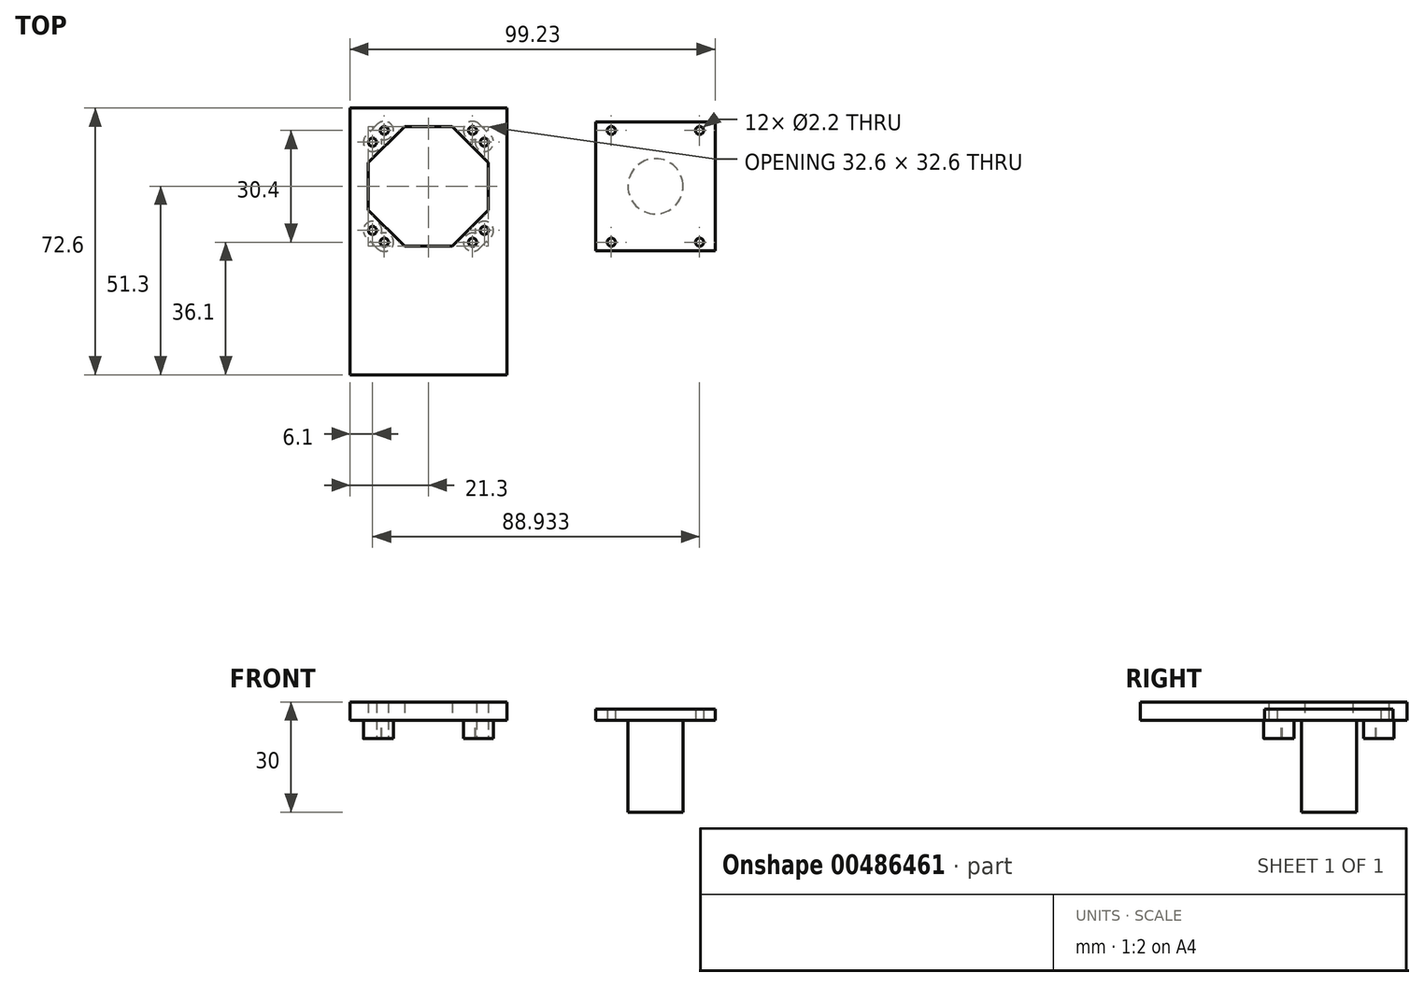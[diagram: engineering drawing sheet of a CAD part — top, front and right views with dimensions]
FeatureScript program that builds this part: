
annotation { "Feature Type Name" : "Feature", "Feature Type Description" : "" }
export const myFeature = defineFeature(function(context is Context, id is Id, definition is map)
    precondition{}
    {
        {
            assignVariable(context, id + "F0", {"name" : "spacer_height", "anyValue" : 5});
        }
        {
            var Q0;
            Q0=qCreatedBy(makeId("Top.planeOp"),FACE);
            var sketch = newSketch(context, id + "F1", { "sketchPlane" : qUnion([Q0])});
            skCircle(sketch, "E0", {"center": v(-12, 15.2) * mm, "radius": 1.1 * mm, "construction": true});
            skCircle(sketch, "E1", {"center": v(-15.2, 12) * mm, "radius": 1.1 * mm, "construction": true});
            skCircle(sketch, "E2.MirrorC", {"center": v(15.2, 12) * mm, "radius": 1.1 * mm, "construction": true});
            skCircle(sketch, "E3.MirrorC", {"center": v(12, 15.2) * mm, "radius": 1.1 * mm, "construction": true});
            skCircle(sketch, "E4.MirrorC", {"center": v(-12, -15.2) * mm, "radius": 1.1 * mm, "construction": true});
            skCircle(sketch, "E5.MirrorC", {"center": v(-15.2, -12) * mm, "radius": 1.1 * mm, "construction": true});
            skCircle(sketch, "E6.MirrorC", {"center": v(12, -15.2) * mm, "radius": 1.1 * mm, "construction": true});
            skCircle(sketch, "E7.MirrorC", {"center": v(15.2, -12) * mm, "radius": 1.1 * mm, "construction": true});
            skArc(sketch, "E8", {"start": v(-14.1, -12) * mm, "mid": v(-15.2, -10.9) * mm, "end": v(-16.3, -12) * mm});
            skArc(sketch, "E9", {"start": v(-12, -16.3) * mm, "mid": v(-10.9, -15.2) * mm, "end": v(-12, -14.1) * mm});
            skArc(sketch, "E10.MirrorCS", {"start": v(14.1, -12) * mm, "mid": v(15.2, -10.9) * mm, "end": v(16.3, -12) * mm});
            skArc(sketch, "E11.MirrorCS", {"start": v(12, -16.3) * mm, "mid": v(10.9, -15.2) * mm, "end": v(12, -14.1) * mm});
            skLineSegment(sketch, "E12", {"start": v(-6.52, 16.3) * mm, "end": v(-16.3, 6.52) * mm});
            skLineSegment(sketch, "E13", {"start": v(-15.2, 12) * mm, "end": v(-12, 15.2) * mm, "construction": true});
            skLineSegment(sketch, "E14", {"start": v(-16.3, 6.52) * mm, "end": v(-16.3, 0) * mm});
            skLineSegment(sketch, "E15", {"start": v(-6.52, 16.3) * mm, "end": v(0, 16.3) * mm});
            skLineSegment(sketch, "E16.MirrorCS", {"start": v(6.52, 16.3) * mm, "end": v(0, 16.3) * mm});
            skLineSegment(sketch, "E17.MirrorCS", {"start": v(6.52, 16.3) * mm, "end": v(16.3, 6.52) * mm});
            skLineSegment(sketch, "E18.MirrorCS", {"start": v(16.3, 6.52) * mm, "end": v(16.3, 0) * mm});
            skLineSegment(sketch, "E19.MirrorCS", {"start": v(16.3, -6.52) * mm, "end": v(16.3, 0) * mm});
            skLineSegment(sketch, "E20.MirrorCS", {"start": v(6.52, -16.3) * mm, "end": v(16.3, -6.52) * mm});
            skLineSegment(sketch, "E21.MirrorCS", {"start": v(6.52, -16.3) * mm, "end": v(0, -16.3) * mm});
            skLineSegment(sketch, "E22.MirrorCS", {"start": v(-6.52, -16.3) * mm, "end": v(0, -16.3) * mm});
            skLineSegment(sketch, "E23.MirrorCS", {"start": v(-6.52, -16.3) * mm, "end": v(-16.3, -6.52) * mm});
            skLineSegment(sketch, "E24.MirrorCS", {"start": v(-16.3, -6.52) * mm, "end": v(-16.3, 0) * mm});
            skCircle(sketch, "E25", {"center": v(-15.2, 12) * mm, "radius": 1.1 * mm});
            skCircle(sketch, "E26", {"center": v(-12, 15.2) * mm, "radius": 1.1 * mm});
            skCircle(sketch, "E27.MirrorC", {"center": v(12, 15.2) * mm, "radius": 1.1 * mm});
            skCircle(sketch, "E28.MirrorC", {"center": v(15.2, 12) * mm, "radius": 1.1 * mm});
            skLineSegment(sketch, "E29.bottom", {"start": v(-21.3, 21.3) * mm, "end": v(21.3, 21.3) * mm});
            skLineSegment(sketch, "E29.top", {"start": v(-21.3, -51.3) * mm, "end": v(21.3, -51.3) * mm});
            skLineSegment(sketch, "E29.left", {"start": v(-21.3, 21.3) * mm, "end": v(-21.3, -51.3) * mm});
            skLineSegment(sketch, "E29.right", {"start": v(21.3, 21.3) * mm, "end": v(21.3, -51.3) * mm});
            skCircle(sketch, "E30", {"center": v(-15.2, -12) * mm, "radius": 1.1 * mm});
            skCircle(sketch, "E31", {"center": v(-12, -15.2) * mm, "radius": 1.1 * mm});
            skCircle(sketch, "E32", {"center": v(12, -15.2) * mm, "radius": 1.1 * mm});
            skCircle(sketch, "E33", {"center": v(15.2, -12) * mm, "radius": 1.1 * mm});
            skSolve(sketch);
        }
        {
            var Q0;
            Q0 = qSketchRegion(id + "F1", true);
            extrude(context, id + "F2", {"entities" : qUnion([Q0]), "depth" : 5 * mm});
        }
        {
            var Q0;
            Q0=makeQuery(id+"F2.opExtrude","CAP_FACE",FACE,{"disambiguationData":[OSD([sQuery(id+"F1.wireOp",EDGE,"E12"),sQuery(id+"F1.wireOp",EDGE,"E14"),sQuery(id+"F1.wireOp",EDGE,"E15"),sQuery(id+"F1.wireOp",EDGE,"E16.MirrorCS"),sQuery(id+"F1.wireOp",EDGE,"E17.MirrorCS"),sQuery(id+"F1.wireOp",EDGE,"E18.MirrorCS"),sQuery(id+"F1.wireOp",EDGE,"E19.MirrorCS"),sQuery(id+"F1.wireOp",EDGE,"E20.MirrorCS"),sQuery(id+"F1.wireOp",EDGE,"E21.MirrorCS"),sQuery(id+"F1.wireOp",EDGE,"E22.MirrorCS"),sQuery(id+"F1.wireOp",EDGE,"E23.MirrorCS"),sQuery(id+"F1.wireOp",EDGE,"E24.MirrorCS"),sQuery(id+"F1.wireOp",EDGE,"E25"),sQuery(id+"F1.wireOp",EDGE,"E26"),sQuery(id+"F1.wireOp",EDGE,"E27.MirrorC"),sQuery(id+"F1.wireOp",EDGE,"E28.MirrorC"),sQuery(id+"F1.wireOp",EDGE,"E29.bottom"),sQuery(id+"F1.wireOp",EDGE,"E29.top"),sQuery(id+"F1.wireOp",EDGE,"E29.left"),sQuery(id+"F1.wireOp",EDGE,"E29.right"),sQuery(id+"F1.wireOp",EDGE,"E30"),sQuery(id+"F1.wireOp",EDGE,"k77yQqxX-UrBX-OhIO-boUt-8GFUiAlRC8bR"),sQuery(id+"F1.wireOp",EDGE,"E31"),sQuery(id+"F1.wireOp",EDGE,"E32"),sQuery(id+"F1.wireOp",EDGE,"LkwF7Hlu-TzS1-PAAf-PXgn-fIDilgAlXOZW"),sQuery(id+"F1.wireOp",EDGE,"E33")])],"isStart":true});
            var sketch = newSketch(context, id + "F3", { "sketchPlane" : qUnion([Q0])});
            skArc(sketch, "E34", {"start": v(12.85, -12.85) * mm, "mid": v(9.56, -15.74) * mm, "end": v(13.77, -16.97) * mm});
            skArc(sketch, "E35", {"start": v(16.97, -13.77) * mm, "mid": v(15.74, -9.56) * mm, "end": v(12.85, -12.85) * mm});
            skLineSegment(sketch, "E36", {"start": v(13.77, -16.97) * mm, "end": v(16.97, -13.77) * mm});
            skLineSegment(sketch, "E37.MirrorCS", {"start": v(-13.77, -16.97) * mm, "end": v(-16.97, -13.77) * mm});
            skArc(sketch, "E38.MirrorCS", {"start": v(-12.85, -12.85) * mm, "mid": v(-9.56, -15.74) * mm, "end": v(-13.77, -16.97) * mm});
            skArc(sketch, "E39.MirrorCS", {"start": v(-16.97, -13.77) * mm, "mid": v(-15.74, -9.56) * mm, "end": v(-12.85, -12.85) * mm});
            skArc(sketch, "E40.MirrorCS", {"start": v(16.97, 13.77) * mm, "mid": v(15.74, 9.56) * mm, "end": v(12.85, 12.85) * mm});
            skArc(sketch, "E41.MirrorCS", {"start": v(12.85, 12.85) * mm, "mid": v(9.56, 15.74) * mm, "end": v(13.77, 16.97) * mm});
            skLineSegment(sketch, "E42.MirrorCS", {"start": v(13.77, 16.97) * mm, "end": v(16.97, 13.77) * mm});
            skArc(sketch, "E43.MirrorCS", {"start": v(-12.85, 12.85) * mm, "mid": v(-9.56, 15.74) * mm, "end": v(-13.77, 16.97) * mm});
            skArc(sketch, "E44.MirrorCS", {"start": v(-16.97, 13.77) * mm, "mid": v(-15.74, 9.56) * mm, "end": v(-12.85, 12.85) * mm});
            skLineSegment(sketch, "E45.MirrorCS", {"start": v(-13.77, 16.97) * mm, "end": v(-16.97, 13.77) * mm});
            skCircle(sketch, "E46", {"center": v(12, -15.2) * mm, "radius": 1.1 * mm});
            skCircle(sketch, "E47", {"center": v(15.2, -12) * mm, "radius": 1.1 * mm});
            skCircle(sketch, "E48.MirrorC", {"center": v(-12, -15.2) * mm, "radius": 1.1 * mm});
            skCircle(sketch, "E49.MirrorC", {"center": v(-15.2, -12) * mm, "radius": 1.1 * mm});
            skCircle(sketch, "E50.MirrorC", {"center": v(15.2, 12) * mm, "radius": 1.1 * mm});
            skCircle(sketch, "E51.MirrorC", {"center": v(12, 15.2) * mm, "radius": 1.1 * mm});
            skCircle(sketch, "E52.MirrorC", {"center": v(-12, 15.2) * mm, "radius": 1.1 * mm});
            skCircle(sketch, "E53.MirrorC", {"center": v(-15.2, 12) * mm, "radius": 1.1 * mm});
            skSolve(sketch);
        }
        {
            var Q0;
            Q0 = qSketchRegion(id + "F3", true);
            extrude(context, id + "F4", {"entities" : qUnion([Q0]), "operationType" : NewBodyOperationType.ADD, "depth" : (getVariable(context, 'spacer_height')) * mm});
        }
        {
            var Q0;
            Q0=qCreatedBy(makeId("Top.planeOp"),FACE);
            var sketch = newSketch(context, id + "F5", { "sketchPlane" : qUnion([Q0])});
            skLineSegment(sketch, "E54.bottom", {"start": v(45.53, 17.5) * mm, "end": v(77.93, 17.5) * mm});
            skLineSegment(sketch, "E54.top", {"start": v(45.53, -17.5) * mm, "end": v(77.93, -17.5) * mm});
            skLineSegment(sketch, "E54.left", {"start": v(45.53, 17.5) * mm, "end": v(45.53, -17.5) * mm});
            skLineSegment(sketch, "E54.right", {"start": v(77.93, 17.5) * mm, "end": v(77.93, -17.5) * mm});
            skPoint(sketch, "E54.middle", {"position": v(61.73, 0) * mm});
            skLineSegment(sketch, "E55.bottom", {"start": v(49.73, 15.2) * mm, "end": v(73.73, 15.2) * mm, "construction": true});
            skLineSegment(sketch, "E55.top", {"start": v(49.73, -15.2) * mm, "end": v(73.73, -15.2) * mm, "construction": true});
            skLineSegment(sketch, "E55.left", {"start": v(49.73, 15.2) * mm, "end": v(49.73, -15.2) * mm, "construction": true});
            skLineSegment(sketch, "E55.right", {"start": v(73.73, 15.2) * mm, "end": v(73.73, -15.2) * mm, "construction": true});
            skCircle(sketch, "E56", {"center": v(73.73, 15.2) * mm, "radius": 1.1 * mm});
            skCircle(sketch, "E57", {"center": v(49.73, 15.2) * mm, "radius": 1.1 * mm});
            skCircle(sketch, "E58", {"center": v(73.73, -15.2) * mm, "radius": 1.1 * mm});
            skCircle(sketch, "E59", {"center": v(49.73, -15.2) * mm, "radius": 1.1 * mm});
            skSolve(sketch);
        }
        {
            var Q0;
            Q0=makeQuery(id+"F5.imprint","IMPRINT",FACE,{"disambiguationData":[TD([[makeQuery(id+"F5.imprint","IMPRINT",EDGE,{"derivedFrom":sQuery(id+"F5.wireOp",EDGE,"E54.bottom")}),-1.0]])]});
            extrude(context, id + "F6", {"entities" : qUnion([Q0]), "depth" : 3 * mm});
        }
        {
            var Q0;
            Q0=makeQuery(id+"F6.opExtrude","CAP_FACE",FACE,{"disambiguationData":[OSD([sQuery(id+"F5.wireOp",EDGE,"E54.bottom"),sQuery(id+"F5.wireOp",EDGE,"E54.top"),sQuery(id+"F5.wireOp",EDGE,"E54.left"),sQuery(id+"F5.wireOp",EDGE,"E54.right"),sQuery(id+"F5.wireOp",EDGE,"E56"),sQuery(id+"F5.wireOp",EDGE,"E57"),sQuery(id+"F5.wireOp",EDGE,"E58"),sQuery(id+"F5.wireOp",EDGE,"E59")])],"isStart":true});
            var sketch = newSketch(context, id + "F7", { "sketchPlane" : qUnion([Q0])});
            skCircle(sketch, "E60", {"center": v(61.73, 0) * mm, "radius": 7.5 * mm});
            skSolve(sketch);
        }
        {
            var Q0;
            Q0 = qSketchRegion(id + "F7", true);
            extrude(context, id + "F8", {"entities" : qUnion([Q0]), "operationType" : NewBodyOperationType.ADD, "depth" : 25 * mm});
        }
    });
